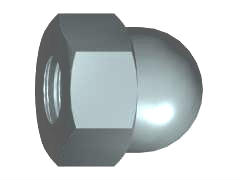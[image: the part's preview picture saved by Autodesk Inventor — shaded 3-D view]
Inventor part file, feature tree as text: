
AUTODESK INVENTOR PART (.ipt)
format: ipt  version: unknown  size: 297,472 bytes
history: native  units: mm (DEFAULTED — no unit token found)
features: other x2, extrude x1, hole x1, chamfer x1, plane x1
ambient origin geometry x7: Origin, YZ Plane, XZ Plane, X Axis, Y Axis, Z Axis, Center Point
feature tree (6):
  extrude  "Körper"  Depth=11.547005mm
  other  "Kopf"
  hole  "Gewinde"  [1 undecoded]
  chamfer  "Fase1"  [1 undecoded]
  other  "Work Axis1"
  plane  "Work Plane1"
note: 2 required parameter values undecoded (feature->parameter linkage not recoverable at this tier; creation-order binding heuristic only, values carry confidence <= 0.55)
